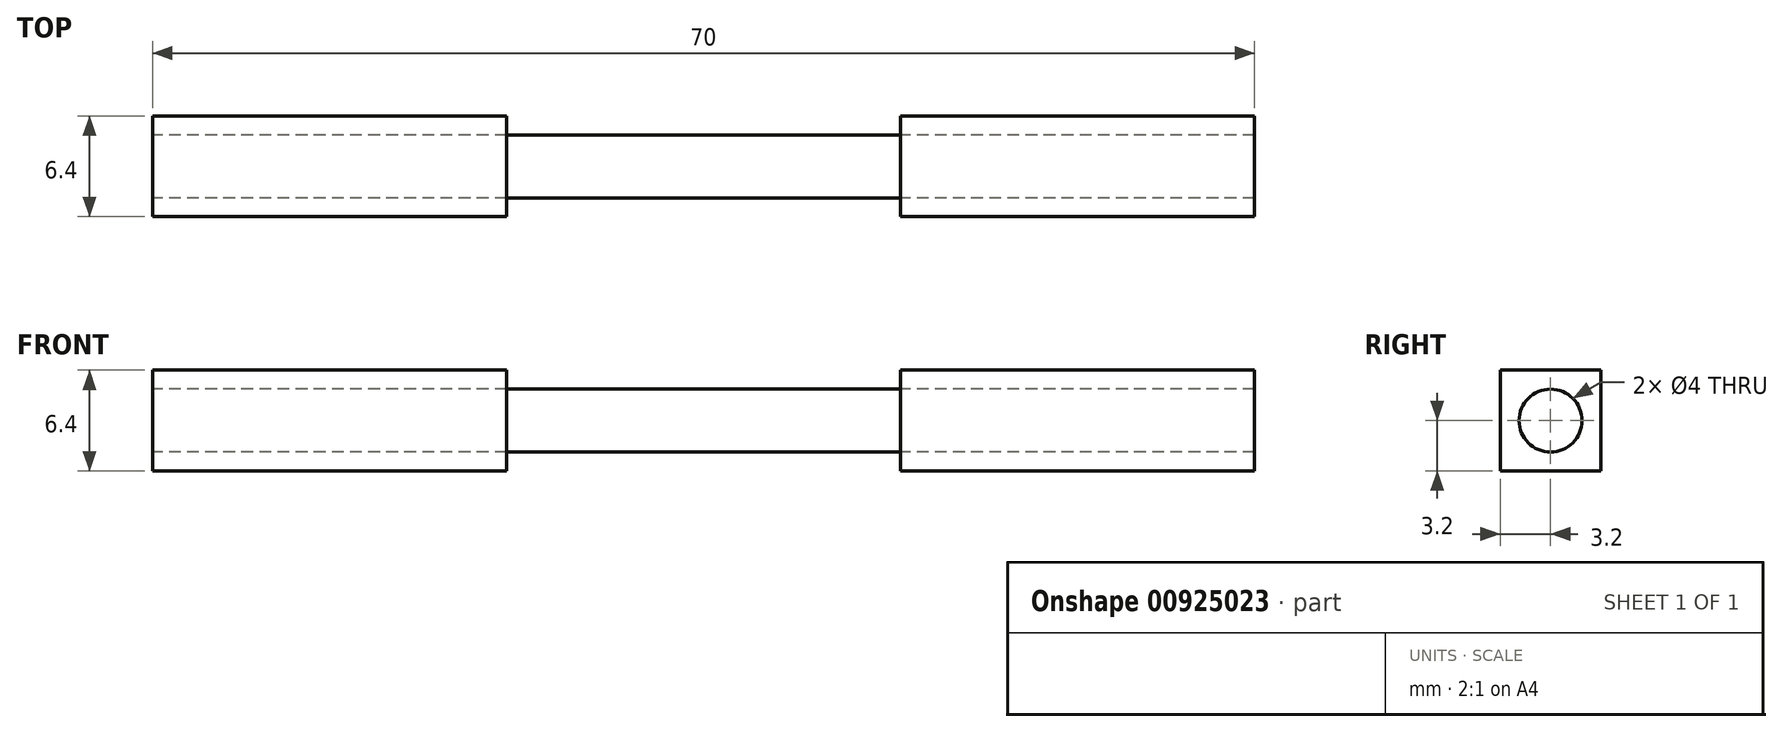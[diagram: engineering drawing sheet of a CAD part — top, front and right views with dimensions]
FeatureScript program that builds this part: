
annotation { "Feature Type Name" : "Feature", "Feature Type Description" : "" }
export const myFeature = defineFeature(function(context is Context, id is Id, definition is map)
    precondition{}
    {
        {
            var Q0;
            Q0=qCreatedBy(makeId("Right.planeOp"),FACE);
            var sketch = newSketch(context, id + "F0", { "sketchPlane" : qUnion([Q0])});
            skLineSegment(sketch, "E0.bottom", {"start": v(-3.2, 3.2) * mm, "end": v(3.2, 3.2) * mm});
            skLineSegment(sketch, "E0.top", {"start": v(-3.2, -3.2) * mm, "end": v(3.2, -3.2) * mm});
            skLineSegment(sketch, "E0.left", {"start": v(-3.2, 3.2) * mm, "end": v(-3.2, -3.2) * mm});
            skLineSegment(sketch, "E0.right", {"start": v(3.2, 3.2) * mm, "end": v(3.2, -3.2) * mm});
            skPoint(sketch, "E0.middle", {"position": v(0, 0) * mm});
            skCircle(sketch, "E1", {"center": v(0, 0) * mm, "radius": 2 * mm});
            skLineSegment(sketch, "E2", {"start": v(3.2, 3.2) * mm, "end": v(-3.2, -3.2) * mm});
            skLineSegment(sketch, "E3", {"start": v(-3.2, 3.2) * mm, "end": v(3.2, -3.2) * mm});
            skSolve(sketch);
        }
        {
            var Q0;
            {var subQ0=sQuery(id+"F0.wireOp",EDGE,"E0.top");Q0=makeQuery(id+"F0.imprint","IMPRINT",FACE,{"disambiguationData":[TD([[makeQuery(id+"F0.imprint","IMPRINT",EDGE,{"derivedFrom":subQ0}),1.0]])]});}
            var Q1;
            {var subQ0=sQuery(id+"F0.wireOp",EDGE,"E0.left");Q1=makeQuery(id+"F0.imprint","IMPRINT",FACE,{"disambiguationData":[TD([[makeQuery(id+"F0.imprint","IMPRINT",EDGE,{"derivedFrom":subQ0}),1.0]])]});}
            var Q2;
            {var subQ0=sQuery(id+"F0.wireOp",EDGE,"E0.right");Q2=makeQuery(id+"F0.imprint","IMPRINT",FACE,{"disambiguationData":[TD([[makeQuery(id+"F0.imprint","IMPRINT",EDGE,{"derivedFrom":subQ0}),-1.0]])]});}
            var Q3;
            {var subQ0=sQuery(id+"F0.wireOp",EDGE,"E0.bottom");Q3=makeQuery(id+"F0.imprint","IMPRINT",FACE,{"disambiguationData":[TD([[makeQuery(id+"F0.imprint","IMPRINT",EDGE,{"derivedFrom":subQ0}),-1.0]])]});}
            extrude(context, id + "F1", {"entities" : qUnion([Q0, Q1, Q2, Q3]), "endBound" : BoundingType.SYMMETRIC, "depth" : 70 * mm, "offsetDistance" : 25 * mm});
        }
        {
            var Q0;
            {var subQ0=sQuery(id+"F0.wireOp",EDGE,"E3");var subQ1=sQuery(id+"F0.wireOp",EDGE,"E1");var subQ2=makeQuery(id+"F0.imprint","INTERSECT",VERTEX,{"disambiguationData":[OD(0.0)],"derivedFrom":[subQ1,subQ0]});Q0=makeQuery(id+"F0.imprint","IMPRINT",FACE,{"disambiguationData":[TD([[makeQuery(id+"F0.imprint","IMPRINT",EDGE,{"disambiguationData":[TD([[subQ2,1.0]])],"derivedFrom":subQ1}),1.0]])]});}
            var Q1;
            {var subQ0=sQuery(id+"F0.wireOp",EDGE,"E2");var subQ1=sQuery(id+"F0.wireOp",EDGE,"E1");var subQ2=makeQuery(id+"F0.imprint","INTERSECT",VERTEX,{"disambiguationData":[OD(0.0)],"derivedFrom":[subQ1,subQ0]});Q1=makeQuery(id+"F0.imprint","IMPRINT",FACE,{"disambiguationData":[TD([[makeQuery(id+"F0.imprint","IMPRINT",EDGE,{"disambiguationData":[TD([[subQ2,1.0]])],"derivedFrom":subQ1}),1.0]])]});}
            var Q2;
            {var subQ0=sQuery(id+"F0.wireOp",EDGE,"E2");var subQ1=sQuery(id+"F0.wireOp",EDGE,"E1");var subQ2=makeQuery(id+"F0.imprint","INTERSECT",VERTEX,{"disambiguationData":[OD(1.0)],"derivedFrom":[subQ1,subQ0]});Q2=makeQuery(id+"F0.imprint","IMPRINT",FACE,{"disambiguationData":[TD([[makeQuery(id+"F0.imprint","IMPRINT",EDGE,{"disambiguationData":[TD([[subQ2,-1.0]])],"derivedFrom":subQ1}),1.0]])]});}
            var Q3;
            {var subQ0=sQuery(id+"F0.wireOp",EDGE,"E3");var subQ1=sQuery(id+"F0.wireOp",EDGE,"E1");var subQ2=makeQuery(id+"F0.imprint","INTERSECT",VERTEX,{"disambiguationData":[OD(0.0)],"derivedFrom":[subQ1,subQ0]});Q3=makeQuery(id+"F0.imprint","IMPRINT",FACE,{"disambiguationData":[TD([[makeQuery(id+"F0.imprint","IMPRINT",EDGE,{"disambiguationData":[TD([[subQ2,-1.0]])],"derivedFrom":subQ1}),1.0]])]});}
            extrude(context, id + "F2", {"entities" : qUnion([Q0, Q1, Q2, Q3]), "endBound" : BoundingType.SYMMETRIC, "depth" : 25 * mm, "offsetDistance" : 25 * mm});
        }
        {
            var Q0;
            {var subQ0=sQuery(id+"F0.wireOp",EDGE,"E0.bottom");Q0=makeQuery(id+"F0.imprint","IMPRINT",FACE,{"disambiguationData":[TD([[makeQuery(id+"F0.imprint","IMPRINT",EDGE,{"derivedFrom":subQ0}),-1.0]])]});}
            var Q1;
            {var subQ0=sQuery(id+"F0.wireOp",EDGE,"E0.left");Q1=makeQuery(id+"F0.imprint","IMPRINT",FACE,{"disambiguationData":[TD([[makeQuery(id+"F0.imprint","IMPRINT",EDGE,{"derivedFrom":subQ0}),1.0]])]});}
            var Q2;
            {var subQ0=sQuery(id+"F0.wireOp",EDGE,"E0.top");Q2=makeQuery(id+"F0.imprint","IMPRINT",FACE,{"disambiguationData":[TD([[makeQuery(id+"F0.imprint","IMPRINT",EDGE,{"derivedFrom":subQ0}),1.0]])]});}
            var Q3;
            {var subQ0=sQuery(id+"F0.wireOp",EDGE,"E0.right");Q3=makeQuery(id+"F0.imprint","IMPRINT",FACE,{"disambiguationData":[TD([[makeQuery(id+"F0.imprint","IMPRINT",EDGE,{"derivedFrom":subQ0}),-1.0]])]});}
            extrude(context, id + "F3", {"entities" : qUnion([Q0, Q1, Q2, Q3]), "operationType" : NewBodyOperationType.REMOVE, "endBound" : BoundingType.SYMMETRIC, "oppositeDirection" : true, "depth" : 25 * mm, "offsetDistance" : 25 * mm});
        }
    });
